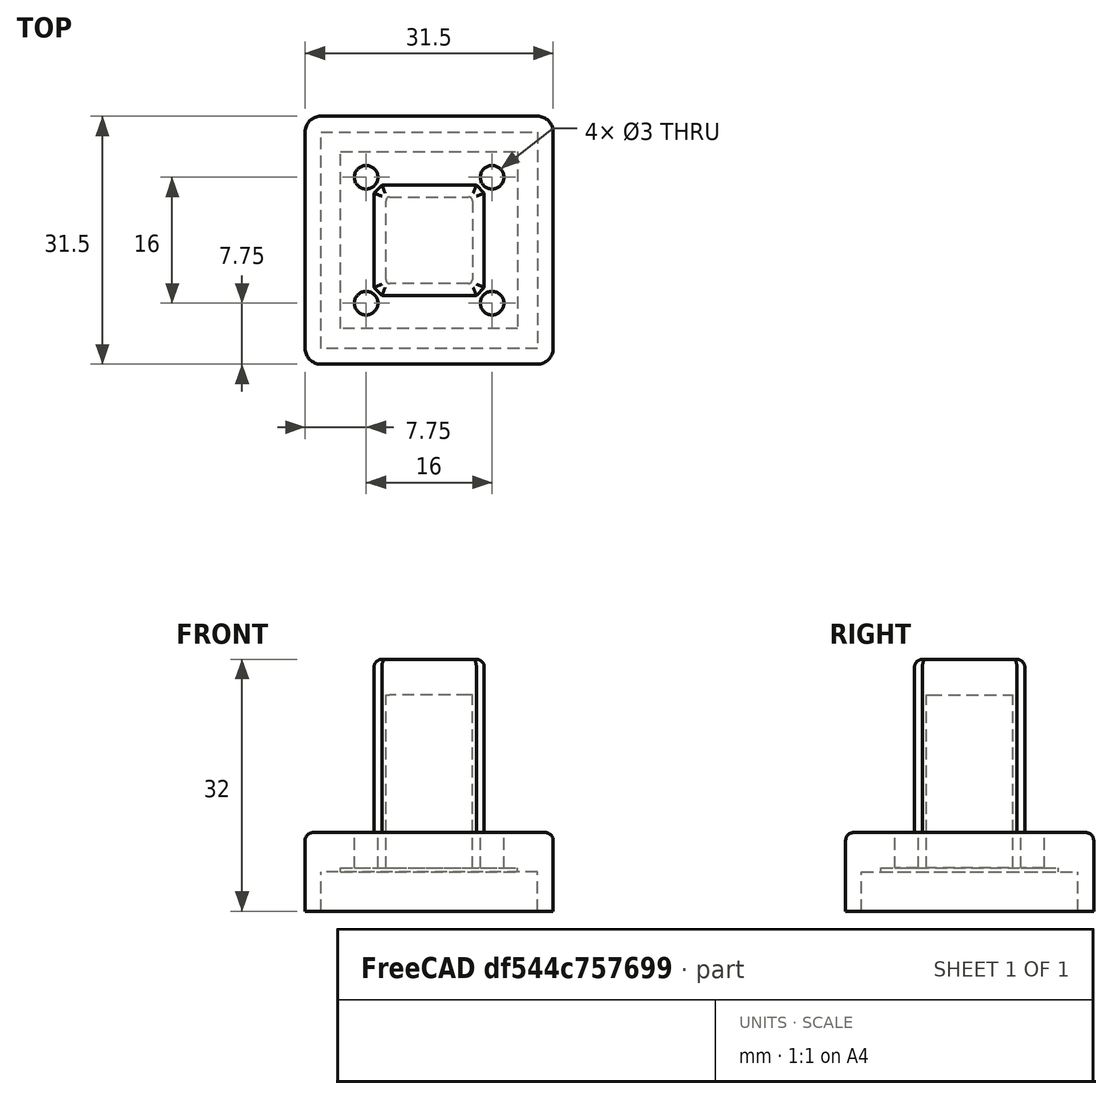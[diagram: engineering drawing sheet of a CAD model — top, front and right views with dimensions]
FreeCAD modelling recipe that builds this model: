
FCSTD DOCUMENT  (FreeCAD 1.1R44874 (Git))
Label: hood1slim_10x10x20_D
objects: Sketcher::SketchObject×7, PartDesign::Pocket×3, PartDesign::Pad×2, PartDesign::Fillet×2, App::Point×1, PartDesign::Hole×1, PartDesign::Body×1, Mesh::Feature×1
note: 39 computed .brp shape members not serialized (recipe doc carries the construction recipe); baked Part::Feature solids carry a one-line shape summary decoded from their .brp

FEATURE [App::Point] Origin001
  Role = Origin
FEATURE [Sketcher::SketchObject] Sketch
  ArcFitTolerance = 1e-06
  AttachmentSupport = -> [Origin]
  ExternalTypes = [0]
  FullyConstrained = true
  MakeInternals = false
  MapMode = 5
  _ExternalGeoVersion = 1
  sketch-geometry (13):
    g0: LineSegment StartX=-13.75 StartY=-15.75 StartZ=0 EndX=13.75 EndY=-15.75 EndZ=0
    g1: LineSegment StartX=15.75 StartY=-13.75 StartZ=0 EndX=15.75 EndY=13.75 EndZ=0
    g2: LineSegment StartX=13.75 StartY=15.75 StartZ=0 EndX=-13.75 EndY=15.75 EndZ=0
    g3: LineSegment StartX=-15.75 StartY=13.75 StartZ=0 EndX=-15.75 EndY=-13.75 EndZ=0
    g4: GeomPoint [constr] X=0 Y=0 Z=0
    g5: ArcOfCircle CenterX=-13.75 CenterY=13.75 CenterZ=0 NormalX=0 NormalY=0 NormalZ=1 AngleXU=0 Radius=2 StartAngle=1.5708 EndAngle=3.14159
    g6: GeomPoint [constr] X=-15.75 Y=15.75 Z=0
    g7: ArcOfCircle CenterX=13.75 CenterY=13.75 CenterZ=0 NormalX=0 NormalY=0 NormalZ=1 AngleXU=0 Radius=2 StartAngle=0 EndAngle=1.5708
    g8: GeomPoint [constr] X=15.75 Y=15.75 Z=0
    g9: ArcOfCircle CenterX=13.75 CenterY=-13.75 CenterZ=0 NormalX=0 NormalY=0 NormalZ=1 AngleXU=0 Radius=2 StartAngle=4.71239 EndAngle=6.28319
    g10: GeomPoint [constr] X=15.75 Y=-15.75 Z=0
    g11: ArcOfCircle CenterX=-13.75 CenterY=-13.75 CenterZ=0 NormalX=0 NormalY=0 NormalZ=1 AngleXU=0 Radius=2 StartAngle=3.14159 EndAngle=4.71239
    g12: GeomPoint [constr] X=-15.75 Y=-15.75 Z=0
  constraints (28):
    c: Horizontal(g0)
    c: Horizontal(g2)
    c: Vertical(g1)
    c: Vertical(g3)
    c: Symmetric(g8,g12,g4)
    c: Distance(g10,g12) = 31.5
    c: Distance(g12,g6) = 31.5
    c: Coincident(g4,g-1)
    c: PointOnObject(g6,g3)
    c: PointOnObject(g6,g2)
    c: Tangent(g3,g5) = -1.5708
    c: Tangent(g2,g5) = -1.5708
    c: Radius(g5) = 2
    c: PointOnObject(g8,g1)
    c: PointOnObject(g8,g2)
    c: Tangent(g1,g7) = -1.5708
    c: Tangent(g2,g7) = -1.5708
    c: PointOnObject(g10,g1)
    c: PointOnObject(g10,g0)
    c: Tangent(g1,g9) = -1.5708
    c: Tangent(g0,g9) = -1.5708
    c: PointOnObject(g12,g0)
    c: PointOnObject(g12,g3)
    c: Tangent(g0,g11) = -1.5708
    c: Tangent(g3,g11) = -1.5708
    c: Equal(g5,g7)
    c: Equal(g5,g11)
    c: Equal(g5,g9)
FEATURE [PartDesign::Pad] Pad
  Direction = (0,0,1)
  Length = 10
  Length2 = 10
  Profile = -> Sketch
  ReferenceAxis = -> Sketch [N_Axis]
  Refine = true
  SideType = 0
  Suppressed = false
  Type = 0
  Type2 = 0
FEATURE [Sketcher::SketchObject] Sketch001
  ArcFitTolerance = 1e-06
  AttachmentSupport = -> [Pad]
  ExternalTypes = [0]
  FullyConstrained = true
  MakeInternals = false
  MapMode = 5
  Placement = pos=(0,0,0) rot=(1,0,0;3.14159rad)
  _ExternalGeoVersion = 1
  sketch-geometry (5):
    g0: LineSegment StartX=-13.75 StartY=-13.75 StartZ=0 EndX=13.75 EndY=-13.75 EndZ=0
    g1: LineSegment StartX=13.75 StartY=-13.75 StartZ=0 EndX=13.75 EndY=13.75 EndZ=0
    g2: LineSegment StartX=13.75 StartY=13.75 StartZ=0 EndX=-13.75 EndY=13.75 EndZ=0
    g3: LineSegment StartX=-13.75 StartY=13.75 StartZ=0 EndX=-13.75 EndY=-13.75 EndZ=0
    g4: GeomPoint [constr] X=0 Y=0 Z=0
  constraints (12):
    c: Coincident(g0,g1)
    c: Coincident(g1,g2)
    c: Coincident(g2,g3)
    c: Coincident(g3,g0)
    c: Horizontal(g0)
    c: Horizontal(g2)
    c: Vertical(g1)
    c: Vertical(g3)
    c: Symmetric(g2,g0,g4)
    c: Distance(g1,g3) = 27.5
    c: Distance(g0,g2) = 27.5
    c: Coincident(g4,g-1)
FEATURE [PartDesign::Pocket] Pocket
  BaseFeature = -> Pad
  Direction = (0,0,1)
  Length = 5
  Length2 = 5
  Profile = -> Sketch001
  ReferenceAxis = -> Sketch001 [N_Axis]
  Refine = true
  SideType = 0
  Suppressed = false
  Type = 0
  Type2 = 0
FEATURE [Sketcher::SketchObject] Sketch002
  ArcFitTolerance = 1e-06
  AttachmentSupport = -> [Pocket]
  ExternalTypes = [0]
  FullyConstrained = true
  MakeInternals = false
  MapMode = 5
  Placement = pos=(0,0,5) rot=(1,0,0;3.14159rad)
  _ExternalGeoVersion = 1
  sketch-geometry (5):
    g0: LineSegment StartX=-11.25 StartY=-11.25 StartZ=0 EndX=11.25 EndY=-11.25 EndZ=0
    g1: LineSegment StartX=11.25 StartY=-11.25 StartZ=0 EndX=11.25 EndY=11.25 EndZ=0
    g2: LineSegment StartX=11.25 StartY=11.25 StartZ=0 EndX=-11.25 EndY=11.25 EndZ=0
    g3: LineSegment StartX=-11.25 StartY=11.25 StartZ=0 EndX=-11.25 EndY=-11.25 EndZ=0
    g4: GeomPoint [constr] X=0 Y=0 Z=0
  constraints (12):
    c: Coincident(g0,g1)
    c: Coincident(g1,g2)
    c: Coincident(g2,g3)
    c: Coincident(g3,g0)
    c: Horizontal(g0)
    c: Horizontal(g2)
    c: Vertical(g1)
    c: Vertical(g3)
    c: Symmetric(g2,g0,g4)
    c: Distance(g1,g3) = 22.5
    c: Distance(g0,g2) = 22.5
    c: Coincident(g4,g-1)
FEATURE [PartDesign::Pocket] Pocket001
  BaseFeature = -> Pocket
  Direction = (0,0,1)
  Length = 0.5
  Length2 = 5
  Profile = -> Sketch002
  ReferenceAxis = -> Sketch002 [N_Axis]
  Refine = true
  SideType = 0
  Suppressed = false
  Type = 0
  Type2 = 0
FEATURE [Sketcher::SketchObject] Sketch003
  ArcFitTolerance = 1e-06
  AttachmentSupport = -> [Pocket001]
  ExternalTypes = [0]
  FullyConstrained = true
  MakeInternals = false
  MapMode = 5
  Placement = pos=(0,0,5.5) rot=(1,0,0;3.14159rad)
  _ExternalGeoVersion = 1
  sketch-geometry (4):
    g0: Circle CenterX=8 CenterY=8 CenterZ=0 NormalX=0 NormalY=0 NormalZ=1 AngleXU=0 Radius=1.5
    g1: Circle CenterX=-8 CenterY=8 CenterZ=0 NormalX=0 NormalY=0 NormalZ=1 AngleXU=0 Radius=1.5
    g2: Circle CenterX=-8 CenterY=-8 CenterZ=0 NormalX=0 NormalY=0 NormalZ=1 AngleXU=0 Radius=1.5
    g3: Circle CenterX=8 CenterY=-8 CenterZ=0 NormalX=0 NormalY=0 NormalZ=1 AngleXU=0 Radius=1.5
  constraints (9):
    c: Diameter(g0) = 3
    c: DistanceY(g-1,g0) = 8
    c: DistanceX(g-1,g0) = 8
    c: Equal(g0,g1)
    c: Equal(g0,g2)
    c: Equal(g0,g3)
    c: Symmetric(g1,g3,g-1)
    c: Symmetric(g0,g3,g-1)
    c: Symmetric(g2,g3,g-2)
FEATURE [PartDesign::Hole] Hole
  BaseFeature = -> Pocket001
  BaseProfileType = 7
  CustomThreadClearance = 0
  Depth = 15
  DepthType = 0
  Diameter = 3
  DrillForDepth = false
  DrillPoint = 1
  DrillPointAngle = 118
  HoleCutCountersinkAngle = 90
  HoleCutCustomValues = false
  HoleCutDepth = 0
  HoleCutDiameter = 0
  HoleCutType = 0
  ModelThread = false
  Profile = -> Sketch003
  Refine = true
  Suppressed = false
  Tapered = false
  TaperedAngle = 90
  ThreadClass = 0
  ThreadDepth = 15
  ThreadDepthType = 0
  ThreadDiameter = 3
  ThreadDirection = 0
  ThreadFit = 0
  ThreadSize = 0
  ThreadType = 0
  Threaded = false
  UseCustomThreadClearance = false
FEATURE [Sketcher::SketchObject] Sketch004
  ArcFitTolerance = 1e-06
  AttachmentSupport = -> [Hole]
  ExternalGeometry = -> [Sketch002]
  ExternalTypes = [0,0,0,0]
  FullyConstrained = true
  MakeInternals = false
  MapMode = 5
  Placement = pos=(0,0,5.5) rot=(1,0,0;3.14159rad)
  _ExternalGeoVersion = 1
  sketch-geometry (21):
    g0: GeomPoint [constr] X=0 Y=0 Z=0
    g1: LineSegment StartX=-11.25 StartY=-5.5 StartZ=0 EndX=-11.25 EndY=5.5 EndZ=0
    g2: LineSegment StartX=-11.25 StartY=5.5 StartZ=0 EndX=-7 EndY=5.5 EndZ=0
    g3: LineSegment StartX=-5.5 StartY=7 StartZ=0 EndX=-5.5 EndY=11.25 EndZ=0
    g4: LineSegment StartX=-5.5 StartY=11.25 StartZ=0 EndX=5.5 EndY=11.25 EndZ=0
    g5: LineSegment StartX=5.5 StartY=11.25 StartZ=0 EndX=5.5 EndY=7 EndZ=0
    g6: LineSegment StartX=7 StartY=5.5 StartZ=0 EndX=11.25 EndY=5.5 EndZ=0
    g7: LineSegment StartX=11.25 StartY=5.5 StartZ=0 EndX=11.25 EndY=-5.5 EndZ=0
    g8: LineSegment StartX=11.25 StartY=-5.5 StartZ=0 EndX=7 EndY=-5.5 EndZ=0
    g9: LineSegment StartX=5.5 StartY=-7 StartZ=0 EndX=5.5 EndY=-11.25 EndZ=0
    g10: LineSegment StartX=5.5 StartY=-11.25 StartZ=0 EndX=-5.5 EndY=-11.25 EndZ=0
    g11: LineSegment StartX=-5.5 StartY=-11.25 StartZ=0 EndX=-5.5 EndY=-7 EndZ=0
    g12: LineSegment StartX=-7 StartY=-5.5 StartZ=0 EndX=-11.25 EndY=-5.5 EndZ=0
    g13: ArcOfCircle CenterX=-7 CenterY=7 CenterZ=0 NormalX=0 NormalY=0 NormalZ=1 AngleXU=0 Radius=1.5 StartAngle=4.71239 EndAngle=6.28319
    g14: GeomPoint [constr] X=-5.5 Y=5.5 Z=0
    g15: ArcOfCircle CenterX=7 CenterY=7 CenterZ=0 NormalX=0 NormalY=0 NormalZ=1 AngleXU=0 Radius=1.5 StartAngle=3.14159 EndAngle=4.71239
    g16: GeomPoint [constr] X=5.5 Y=5.5 Z=0
    g17: ArcOfCircle CenterX=7 CenterY=-7 CenterZ=0 NormalX=0 NormalY=0 NormalZ=1 AngleXU=0 Radius=1.5 StartAngle=1.5708 EndAngle=3.14159
    g18: GeomPoint [constr] X=5.5 Y=-5.5 Z=0
    g19: ArcOfCircle CenterX=-7 CenterY=-7 CenterZ=0 NormalX=0 NormalY=0 NormalZ=1 AngleXU=0 Radius=1.5 StartAngle=0 EndAngle=1.5708
    g20: GeomPoint [constr] X=-5.5 Y=-5.5 Z=0
  constraints (46):
    c: Coincident(g0,g-1)
    c: Coincident(g1,g2)
    c: Horizontal(g2)
    c: Vertical(g3)
    c: Coincident(g3,g4)
    c: Coincident(g4,g5)
    c: Vertical(g5)
    c: Horizontal(g6)
    c: Coincident(g6,g7)
    c: Coincident(g7,g8)
    c: Vertical(g9)
    c: Coincident(g9,g10)
    c: Coincident(g10,g11)
    c: Coincident(g12,g1)
    c: Tangent(g4,g-3)
    c: Tangent(g1,g-4)
    c: Tangent(g7,g-6)
    c: Tangent(g10,g-5)
    c: DistanceY(g-1,g16) = 5.5
    c: DistanceX(g-1,g16) = 5.5
    c: Symmetric(g16,g18,g-1)
    c: Symmetric(g16,g14,g-2)
    c: Symmetric(g18,g20,g-2)
    c: Parallel(g6,g8)
    c: Parallel(g2,g12)
    c: Parallel(g9,g11)
    c: PointOnObject(g14,g3)
    c: PointOnObject(g14,g2)
    c: Tangent(g3,g13) = -1.5708
    c: Tangent(g2,g13) = -1.5708
    c: Radius(g13) = 1.5
    c: PointOnObject(g16,g5)
    c: PointOnObject(g16,g6)
    c: Tangent(g5,g15) = -1.5708
    c: Tangent(g6,g15) = -1.5708
    c: PointOnObject(g18,g8)
    c: PointOnObject(g18,g9)
    c: Tangent(g8,g17) = -1.5708
    c: Tangent(g9,g17) = -1.5708
    c: PointOnObject(g20,g12)
    c: PointOnObject(g20,g11)
    c: Tangent(g12,g19) = -1.5708
    c: Tangent(g11,g19) = -1.5708
    c: Equal(g13,g15)
    c: Equal(g13,g19)
    c: Equal(g13,g17)
FEATURE [Sketcher::SketchObject] Sketch005
  ArcFitTolerance = 1e-06
  AttachmentSupport = -> [Hole]
  ExternalTypes = [0]
  FullyConstrained = true
  MakeInternals = false
  MapMode = 5
  Placement = pos=(0,0,10) rot=(0,0,1;0rad)
  _ExternalGeoVersion = 1
  sketch-geometry (17):
    g0: LineSegment StartX=-6 StartY=-7 StartZ=0 EndX=6 EndY=-7 EndZ=0
    g1: LineSegment StartX=7 StartY=-6 StartZ=0 EndX=7 EndY=6 EndZ=0
    g2: LineSegment StartX=6 StartY=7 StartZ=0 EndX=-6 EndY=7 EndZ=0
    g3: LineSegment StartX=-7 StartY=6 StartZ=0 EndX=-7 EndY=-6 EndZ=0
    g4: GeomPoint [constr] X=0 Y=0 Z=0
    g5: ArcOfCircle [constr] CenterX=-6 CenterY=6 CenterZ=0 NormalX=0 NormalY=0 NormalZ=1 AngleXU=0 Radius=1 StartAngle=1.5708 EndAngle=3.14159
    g6: GeomPoint [constr] X=-7 Y=7 Z=0
    g7: LineSegment StartX=-6 StartY=7 StartZ=0 EndX=-7 EndY=6 EndZ=0
    g8: ArcOfCircle [constr] CenterX=6 CenterY=-6 CenterZ=0 NormalX=0 NormalY=0 NormalZ=1 AngleXU=0 Radius=1 StartAngle=4.71239 EndAngle=6.28319
    g9: GeomPoint [constr] X=7 Y=-7 Z=0
    g10: LineSegment StartX=6 StartY=-7 StartZ=0 EndX=7 EndY=-6 EndZ=0
    g11: ArcOfCircle [constr] CenterX=6 CenterY=6 CenterZ=0 NormalX=0 NormalY=0 NormalZ=1 AngleXU=0 Radius=1 StartAngle=0 EndAngle=1.5708
    g12: GeomPoint [constr] X=7 Y=7 Z=0
    g13: LineSegment StartX=7 StartY=6 StartZ=0 EndX=6 EndY=7 EndZ=0
    g14: ArcOfCircle [constr] CenterX=-6 CenterY=-6 CenterZ=0 NormalX=0 NormalY=0 NormalZ=1 AngleXU=0 Radius=1 StartAngle=3.14159 EndAngle=4.71239
    g15: GeomPoint [constr] X=-7 Y=-7 Z=0
    g16: LineSegment StartX=-7 StartY=-6 StartZ=0 EndX=-6 EndY=-7 EndZ=0
  constraints (36):
    c: Horizontal(g0)
    c: Horizontal(g2)
    c: Vertical(g1)
    c: Vertical(g3)
    c: Symmetric(g12,g15,g4)
    c: Distance(g9,g15) = 14
    c: Distance(g15,g6) = 14
    c: Coincident(g4,g-1)
    c: PointOnObject(g6,g3)
    c: PointOnObject(g6,g2)
    c: Tangent(g3,g5) = -1.5708
    c: Tangent(g2,g5) = -1.5708
    c: Coincident(g7,g3)
    c: Coincident(g7,g2)
    c: PointOnObject(g9,g1)
    c: PointOnObject(g9,g0)
    c: Tangent(g1,g8) = -1.5708
    c: Tangent(g0,g8) = -1.5708
    c: Coincident(g10,g1)
    c: Coincident(g10,g0)
    c: Equal(g7,g10)
    c: DistanceY(g4,g3) = 6
    c: PointOnObject(g12,g2)
    c: PointOnObject(g12,g1)
    c: Tangent(g2,g11) = -1.5708
    c: Tangent(g1,g11) = -1.5708
    c: Coincident(g13,g2)
    c: Coincident(g13,g1)
    c: Equal(g7,g13)
    c: PointOnObject(g15,g0)
    c: PointOnObject(g15,g3)
    c: Tangent(g0,g14) = -1.5708
    c: Tangent(g3,g14) = -1.5708
    c: Coincident(g16,g0)
    c: Coincident(g16,g3)
    c: Equal(g7,g16)
FEATURE [PartDesign::Pad] Pad001
  BaseFeature = -> Hole
  Direction = (0,0,1)
  Length = 22
  Length2 = 10
  Profile = -> Sketch005
  ReferenceAxis = -> Sketch005 [N_Axis]
  Refine = true
  SideType = 0
  Suppressed = false
  Type = 0
  Type2 = 0
FEATURE [Sketcher::SketchObject] Sketch006
  ArcFitTolerance = 1e-06
  AttachmentSupport = -> [Pad001]
  ExternalTypes = [0]
  FullyConstrained = true
  MakeInternals = false
  MapMode = 5
  Placement = pos=(0,0,5.5) rot=(1,0,0;3.14159rad)
  _ExternalGeoVersion = 1
  sketch-geometry (10):
    g0: LineSegment StartX=-5 StartY=-5.5 StartZ=0 EndX=5 EndY=-5.5 EndZ=0
    g1: LineSegment StartX=5.5 StartY=-5 StartZ=0 EndX=5.5 EndY=5 EndZ=0
    g2: LineSegment StartX=5 StartY=5.5 StartZ=0 EndX=-5 EndY=5.5 EndZ=0
    g3: LineSegment StartX=-5.5 StartY=5 StartZ=0 EndX=-5.5 EndY=-5 EndZ=0
    g4: ArcOfCircle CenterX=-5 CenterY=-5 CenterZ=0 NormalX=0 NormalY=0 NormalZ=1 AngleXU=0 Radius=0.5 StartAngle=3.14159 EndAngle=4.71239
    g5: ArcOfCircle CenterX=5 CenterY=-5 CenterZ=0 NormalX=0 NormalY=0 NormalZ=1 AngleXU=0 Radius=0.5 StartAngle=4.71239 EndAngle=6.28319
    g6: ArcOfCircle CenterX=5 CenterY=5 CenterZ=0 NormalX=0 NormalY=0 NormalZ=1 AngleXU=0 Radius=0.5 StartAngle=0 EndAngle=1.5708
    g7: ArcOfCircle CenterX=-5 CenterY=5 CenterZ=0 NormalX=0 NormalY=0 NormalZ=1 AngleXU=0 Radius=0.5 StartAngle=1.5708 EndAngle=3.14159
    g8: GeomPoint [constr] X=5.5 Y=5.5 Z=0
    g9: GeomPoint [constr] X=0 Y=0 Z=0
  constraints (22):
    c: Tangent(g0,g4) = -1.5708
    c: Tangent(g0,g5) = -1.5708
    c: Tangent(g1,g5) = -1.5708
    c: Tangent(g1,g6) = -1.5708
    c: Tangent(g2,g6) = -1.5708
    c: Tangent(g2,g7) = -1.5708
    c: Tangent(g3,g7) = -1.5708
    c: Tangent(g3,g4) = -1.5708
    c: Horizontal(g0)
    c: Horizontal(g2)
    c: Vertical(g1)
    c: Vertical(g3)
    c: Equal(g4,g5)
    c: Equal(g5,g6)
    c: Equal(g6,g7)
    c: Symmetric(g2,g0,g9)
    c: PointOnObject(g8,g1)
    c: PointOnObject(g8,g2)
    c: Distance(g1,g3) = 11
    c: Distance(g0,g2) = 11
    c: Radius(g5) = 0.5
    c: Coincident(g9,g-1)
FEATURE [PartDesign::Pocket] Pocket002
  BaseFeature = -> Pad001
  Direction = (0,0,1)
  Length = 22
  Length2 = 5
  Profile = -> Sketch006
  ReferenceAxis = -> Sketch006 [N_Axis]
  Refine = true
  SideType = 0
  Suppressed = false
  Type = 0
  Type2 = 0
FEATURE [PartDesign::Fillet] Fillet
  Base = -> Pocket002 [Face29]
  BaseFeature = -> Pocket002
  Radius = 1
  Refine = true
  SupportTransform = false
  Suppressed = false
  UseAllEdges = false
FEATURE [PartDesign::Fillet] Fillet001
  Base = -> Fillet [Edge18]
  BaseFeature = -> Fillet
  Radius = 1
  Refine = true
  SupportTransform = false
  Suppressed = false
  UseAllEdges = false
FEATURE [PartDesign::Body] Body
  AllowCompound = true
  Group = -> [Sketch,Pad,Sketch001,Pocket,Sketch002,Pocket001,Sketch003,Hole,Sketch004,Sketch005,Pad001,Sketch006,Pocket002,Fillet,Fillet001]
  Origin = -> Origin
  Tip = -> Fillet001
FEATURE [Mesh::Feature] Mesh  label="Body (Meshed)"
